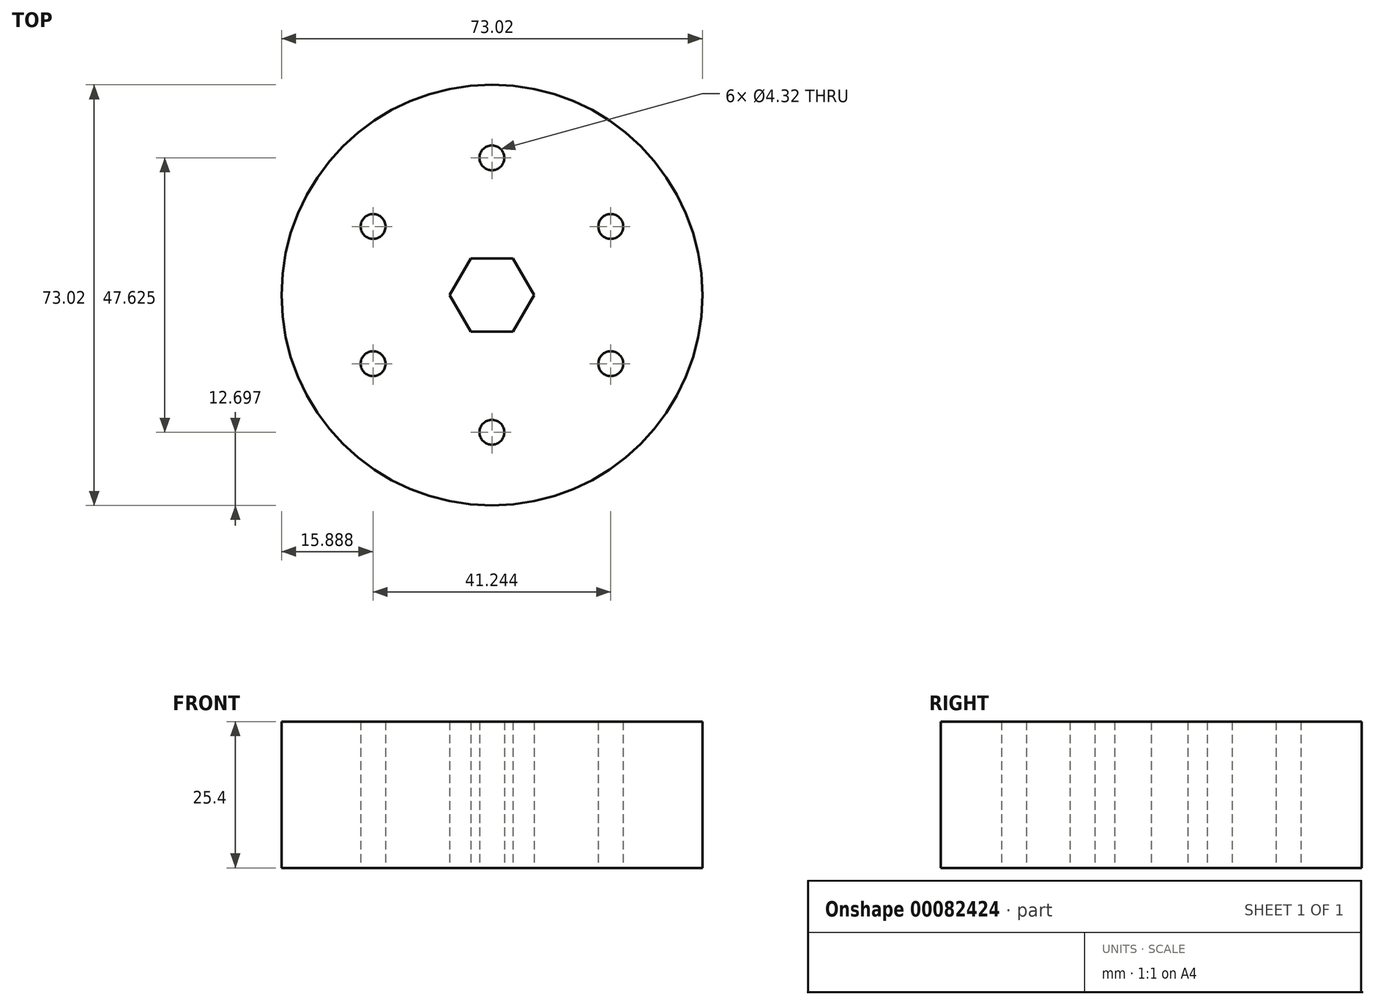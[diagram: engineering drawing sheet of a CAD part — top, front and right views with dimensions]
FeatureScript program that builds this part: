
annotation { "Feature Type Name" : "Feature", "Feature Type Description" : "" }
export const myFeature = defineFeature(function(context is Context, id is Id, definition is map)
    precondition{}
    {
        {
            var Q0;
            Q0=qCreatedBy(makeId("Top.planeOp"),FACE);
            var sketch = newSketch(context, id + "F0", { "sketchPlane" : qUnion([Q0])});
            skCircle(sketch, "E0", {"center": v(0, 0) * mm, "radius": 36.51 * mm});
            skCircle(sketch, "E1.cCircle", {"center": v(0, 0) * mm, "radius": 23.81 * mm, "construction": true});
            skLineSegment(sketch, "E1.0", {"start": v(0, 23.81) * mm, "end": v(20.62, 11.9) * mm, "construction": true});
            skLineSegment(sketch, "E1.1", {"start": v(20.62, 11.9) * mm, "end": v(20.62, -11.9) * mm, "construction": true});
            skLineSegment(sketch, "E1.2", {"start": v(20.62, -11.9) * mm, "end": v(0, -23.81) * mm, "construction": true});
            skLineSegment(sketch, "E1.3", {"start": v(0, -23.81) * mm, "end": v(-20.62, -11.9) * mm, "construction": true});
            skLineSegment(sketch, "E1.4", {"start": v(-20.62, -11.9) * mm, "end": v(-20.62, 11.9) * mm, "construction": true});
            skLineSegment(sketch, "E1.5", {"start": v(-20.62, 11.9) * mm, "end": v(0, 23.81) * mm, "construction": true});
            skCircle(sketch, "E2", {"center": v(0, 23.81) * mm, "radius": 2.16 * mm});
            skCircle(sketch, "E3", {"center": v(20.62, 11.9) * mm, "radius": 2.16 * mm});
            skCircle(sketch, "E4", {"center": v(20.62, -11.9) * mm, "radius": 2.16 * mm});
            skCircle(sketch, "E5", {"center": v(0, -23.81) * mm, "radius": 2.16 * mm});
            skCircle(sketch, "E6", {"center": v(-20.62, -11.9) * mm, "radius": 2.16 * mm});
            skCircle(sketch, "E7", {"center": v(-20.62, 11.9) * mm, "radius": 2.16 * mm});
            skCircle(sketch, "E8.cCircle", {"center": v(0, 0) * mm, "radius": 6.35 * mm, "construction": true});
            skLineSegment(sketch, "E8.0", {"start": v(3.67, -6.35) * mm, "end": v(-3.67, -6.35) * mm});
            skLineSegment(sketch, "E8.1", {"start": v(-3.67, -6.35) * mm, "end": v(-7.33, 0) * mm});
            skLineSegment(sketch, "E8.2", {"start": v(-7.33, 0) * mm, "end": v(-3.67, 6.35) * mm});
            skLineSegment(sketch, "E8.3", {"start": v(-3.67, 6.35) * mm, "end": v(3.67, 6.35) * mm});
            skLineSegment(sketch, "E8.4", {"start": v(3.67, 6.35) * mm, "end": v(7.33, 0) * mm});
            skLineSegment(sketch, "E8.5", {"start": v(7.33, 0) * mm, "end": v(3.67, -6.35) * mm});
            skPoint(sketch, "E8.0.midPoint", {"position": v(0, -6.35) * mm});
            skSolve(sketch);
        }
        {
            var Q0;
            Q0=makeQuery(id+"F0.imprint","IMPRINT",FACE,{"disambiguationData":[TD([[makeQuery(id+"F0.imprint","IMPRINT",EDGE,{"derivedFrom":sQuery(id+"F0.wireOp",EDGE,"E0")}),1.0]])]});
            extrude(context, id + "F1", {"entities" : qUnion([Q0]), "depth" : 25.4 * mm});
        }
    });
